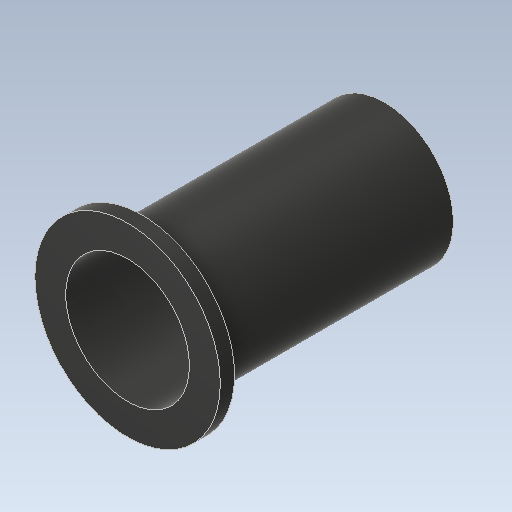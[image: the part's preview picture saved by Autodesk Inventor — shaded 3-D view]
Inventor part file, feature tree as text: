
AUTODESK INVENTOR PART (.ipt)
format: ipt  version: 2021 (Build 250183000, 183)  size: 130,048 bytes
history: native  units: mm
features: extrude x3, sketch x3
ambient origin geometry x8: Origin, YZ Plane, XZ Plane, XY Plane, X Axis, Y Axis, Z Axis, Center Point
bodies: Solid1 (feature_tree)
feature tree (6):
  extrude  "Extrusion1"  Depth=51.0mm TaperAngle=0.0deg
  extrude  "Extrusion2"  Depth=3.0mm TaperAngle=0.0deg
  extrude  "Extrusion3"  Depth=36.75mm TaperAngle=0.0deg
  sketch  "Sketch1"  dims[d0=29.0mm d1=51.0mm d2=0.0mm]
  sketch  "Sketch2"  dims[d3=5.0mm d4=3.0mm d5=0.0mm]
  sketch  "Sketch4"  dims[d44=26.0mm d45=36.75mm d46=0.0mm]
